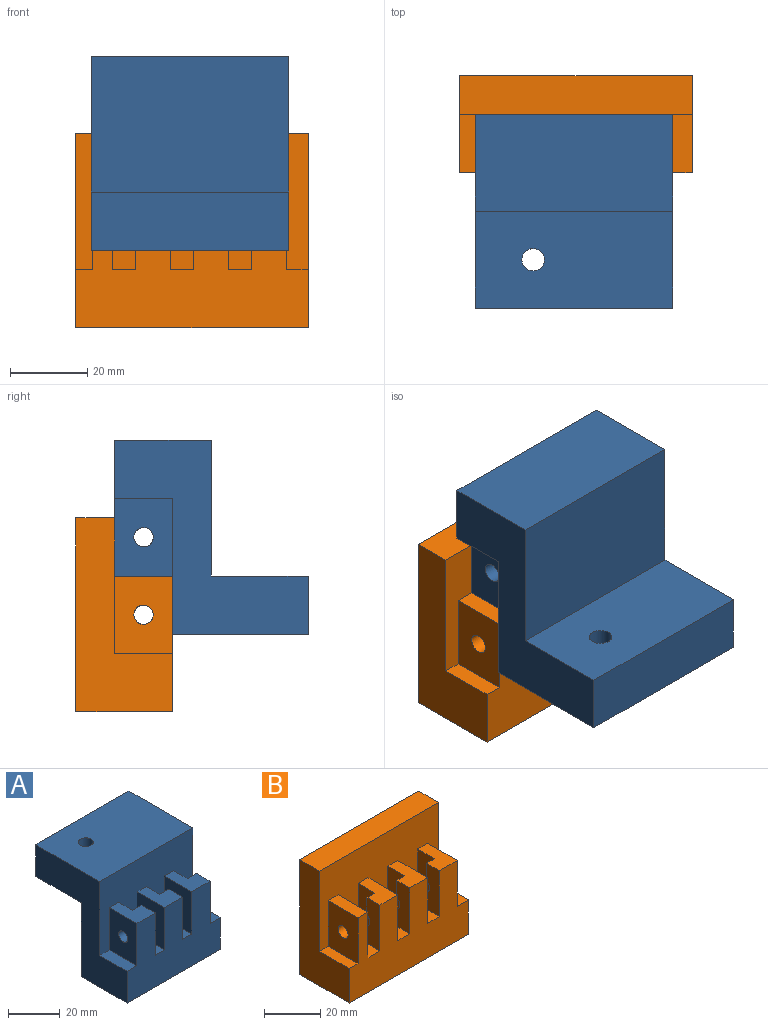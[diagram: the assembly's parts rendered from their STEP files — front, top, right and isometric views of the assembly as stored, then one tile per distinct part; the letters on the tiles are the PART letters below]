
ASSEMBLY  parts=2 mates=1
PART A: 35 faces, bbox 51x50x50 mm
  f0: plane 50.97x35mm, normal (0,1,0), area 1783.8mm2, adj f5,f11,f28,f32
  f1: plane 7.5x5mm, normal (0,1,0), area 37.5mm2, adj f10,f14,f16,f31
  f2: plane 7.5x5mm, normal (0,1,0), area 37.5mm2, adj f9,f19,f21,f30
  f3: plane 7.5x5mm, normal (0,1,0), area 37.5mm2, adj f12,f24,f26,f29
  f4: plane 50.97x35mm, normal (0,0,1), area 1757.4mm2, adj f6,f11,f28,f33,f34
  f5: plane 50.97x25mm, normal (0,0,-1), area 1274.2mm2, adj f0,f8,f11,f28
  f6: plane 50.97x35mm, normal (0,-1,0), area 1483.8mm2, adj f4,f7,f9,f10,f11,f12,f13,f16
  f7: plane 15x5.39mm, normal (0,0,1), area 80.9mm2, adj f6,f8,f13,f28
  f8: plane 50.97x35mm, normal (0,-1,0), area 1364.5mm2, adj f5,f7,f9,f10,f11,f12,f13,f14
  f9: plane 15x10mm, normal (0,0,1), area 112.5mm2, adj f2,f6,f8,f19,f21,f23
  f10: plane 15x10mm, normal (0,0,1), area 112.5mm2, adj f1,f6,f8,f14,f16,f18
  f11: plane 50x50mm, normal (1,0,0), area 1100mm2, adj f0,f4,f5,f6,f8,f12,f32,f33
  f12: plane 15x10.57mm, normal (0,0,1), area 121.1mm2, adj f3,f6,f8,f11,f24,f26
  f13: plane 20x15mm, normal (-1,0,0), area 280.4mm2, adj f6,f7,f8,f17,f31
  f14: plane 20x7.5mm, normal (1,0,0), area 140.2mm2, adj f1,f8,f10,f15,f17,f31
  f15: plane 7.5x5mm, normal (0,1,0), area 37.5mm2, adj f14,f16,f17,f31
  f16: plane 20x7.5mm, normal (1,0,0), area 140.2mm2, adj f1,f6,f10,f15,f17,f31
  f17: plane 15x10mm, normal (0,0,1), area 112.5mm2, adj f6,f8,f13,f14,f15,f16
  f18: plane 20x15mm, normal (-1,0,0), area 280.4mm2, adj f6,f8,f10,f22,f30
  f19: plane 20x7.5mm, normal (1,0,0), area 140.2mm2, adj f2,f8,f9,f20,f22,f30
  f20: plane 7.5x5mm, normal (0,1,0), area 37.5mm2, adj f19,f21,f22,f30
  f21: plane 20x7.5mm, normal (1,0,0), area 140.2mm2, adj f2,f6,f9,f20,f22,f30
  f22: plane 15x10mm, normal (0,0,1), area 112.5mm2, adj f6,f8,f18,f19,f20,f21
  f23: plane 20x15mm, normal (-1,0,0), area 280.4mm2, adj f6,f8,f9,f27,f29
  f24: plane 20x7.5mm, normal (1,0,0), area 140.2mm2, adj f3,f8,f12,f25,f27,f29
  f25: plane 7.5x5mm, normal (0,1,0), area 37.5mm2, adj f24,f26,f27,f29
  f26: plane 20x7.5mm, normal (1,0,0), area 140.2mm2, adj f3,f6,f12,f25,f27,f29
  f27: plane 15x10mm, normal (0,0,1), area 112.5mm2, adj f6,f8,f23,f24,f25,f26
  f28: plane 50x50mm, normal (-1,0,0), area 1100mm2, adj f0,f4,f5,f6,f7,f8,f32,f33
  f29: cylinder r=2.5mm len=10mm, axis (-1,0,0), area 117.8mm2, adj f3,f23,f24,f25,f26
  f30: cylinder r=2.5mm len=10mm, axis (-1,0,0), area 117.8mm2, adj f2,f18,f19,f20,f21
  f31: cylinder r=2.5mm len=10mm, axis (-1,0,0), area 117.8mm2, adj f1,f13,f14,f15,f16
  f32: plane 50.97x25mm, normal (0,0,-1), area 1247.8mm2, adj f0,f11,f28,f33,f34
  f33: plane 50.97x15mm, normal (0,1,0), area 764.5mm2, adj f4,f11,f28,f32
  f34: cylinder r=2.9mm len=15mm, axis (0,0,-1), area 273.3mm2, adj f4,f32
PART B: 37 faces, bbox 60x25x50 mm
  f0: plane 7.71x4mm, normal (0,1,0), area 30.8mm2, adj f7,f16,f18,f36
  f1: plane 7.71x4mm, normal (0,1,0), area 30.8mm2, adj f6,f21,f23,f35
  f2: plane 7.71x4mm, normal (0,1,0), area 30.8mm2, adj f5,f26,f28,f34
  f3: plane 15x4.43mm, normal (0,0,1), area 66.4mm2, adj f4,f8,f13,f30
  f4: plane 60x35mm, normal (0,-1,0), area 1700mm2, adj f3,f5,f6,f7,f8,f9,f11,f14
  f5: plane 15x10mm, normal (0,0,1), area 124mm2, adj f2,f4,f13,f20,f26,f28
  f6: plane 15x10mm, normal (0,0,1), area 124mm2, adj f1,f4,f13,f15,f21,f23
  f7: plane 15x10mm, normal (0,0,1), area 124mm2, adj f0,f4,f13,f16,f18,f31
  f8: plane 50x25mm, normal (-1,0,0), area 725mm2, adj f3,f4,f10,f11,f12,f13
  f9: plane 50x25mm, normal (1,0,0), area 725mm2, adj f4,f10,f11,f12,f13,f14
  f10: plane 60x50mm, normal (0,1,0), area 3000mm2, adj f8,f9,f11,f12
  f11: plane 60x10mm, normal (0,0,1), area 600mm2, adj f4,f8,f9,f10
  f12: plane 60x25mm, normal (0,0,-1), area 1500mm2, adj f8,f9,f10,f13
  f13: plane 60x35mm, normal (0,-1,0), area 1540mm2, adj f3,f5,f6,f7,f8,f9,f12,f14
  f14: plane 15x5.57mm, normal (0,0,1), area 83.6mm2, adj f4,f9,f13,f25
  f15: plane 20x15mm, normal (1,0,0), area 280.4mm2, adj f4,f6,f13,f19,f36
  f16: plane 20x8.5mm, normal (-1,0,0), area 155.3mm2, adj f0,f4,f7,f17,f19,f36
  f17: plane 7.71x4mm, normal (0,1,0), area 30.8mm2, adj f16,f18,f19,f36
  f18: plane 20x6.5mm, normal (-1,0,0), area 125mm2, adj f0,f7,f13,f17,f19,f36
  f19: plane 15x9mm, normal (0,0,1), area 101mm2, adj f4,f13,f15,f16,f17,f18
  f20: plane 20x15mm, normal (1,0,0), area 280.4mm2, adj f4,f5,f13,f24,f35
  f21: plane 20x8.5mm, normal (-1,0,0), area 155.3mm2, adj f1,f4,f6,f22,f24,f35
  f22: plane 7.71x4mm, normal (0,1,0), area 30.8mm2, adj f21,f23,f24,f35
  f23: plane 20x6.5mm, normal (-1,0,0), area 125mm2, adj f1,f6,f13,f22,f24,f35
  f24: plane 15x9mm, normal (0,0,1), area 101mm2, adj f4,f13,f20,f21,f22,f23
  f25: plane 20x15mm, normal (1,0,0), area 280.4mm2, adj f4,f13,f14,f29,f34
  f26: plane 20x8.5mm, normal (-1,0,0), area 155.3mm2, adj f2,f4,f5,f27,f29,f34
  f27: plane 7.71x4mm, normal (0,1,0), area 30.8mm2, adj f26,f28,f29,f34
  f28: plane 20x6.5mm, normal (-1,0,0), area 125mm2, adj f2,f5,f13,f27,f29,f34
  f29: plane 15x9mm, normal (0,0,1), area 101mm2, adj f4,f13,f25,f26,f27,f28
  f30: plane 20x15mm, normal (-1,0,0), area 280.4mm2, adj f3,f4,f13,f32,f33
  f31: plane 20x15mm, normal (1,0,0), area 280.4mm2, adj f4,f7,f13,f32,f33
  f32: plane 15x5mm, normal (0,0,1), area 75mm2, adj f4,f13,f30,f31
  f33: cylinder r=2.5mm len=5mm, axis (-1,0,0), area 78.5mm2, adj f30,f31
  f34: cylinder r=2.5mm len=9mm, axis (-1,0,0), area 101.7mm2, adj f2,f25,f26,f27,f28
  f35: cylinder r=2.5mm len=9mm, axis (-1,0,0), area 101.7mm2, adj f1,f20,f21,f22,f23
  f36: cylinder r=2.5mm len=9mm, axis (-1,0,0), area 101.7mm2, adj f0,f15,f16,f17,f18
PLACE A rot(axis=(1,0,0),180deg) t=(-12.04,-17.8,70)mm
PLACE B t=(-7.04,-15.59,0)mm fixed
MATE slider A.f27 <-> B.f5  axis (0,0,-1) through (28.35,-9.19,35)mm
